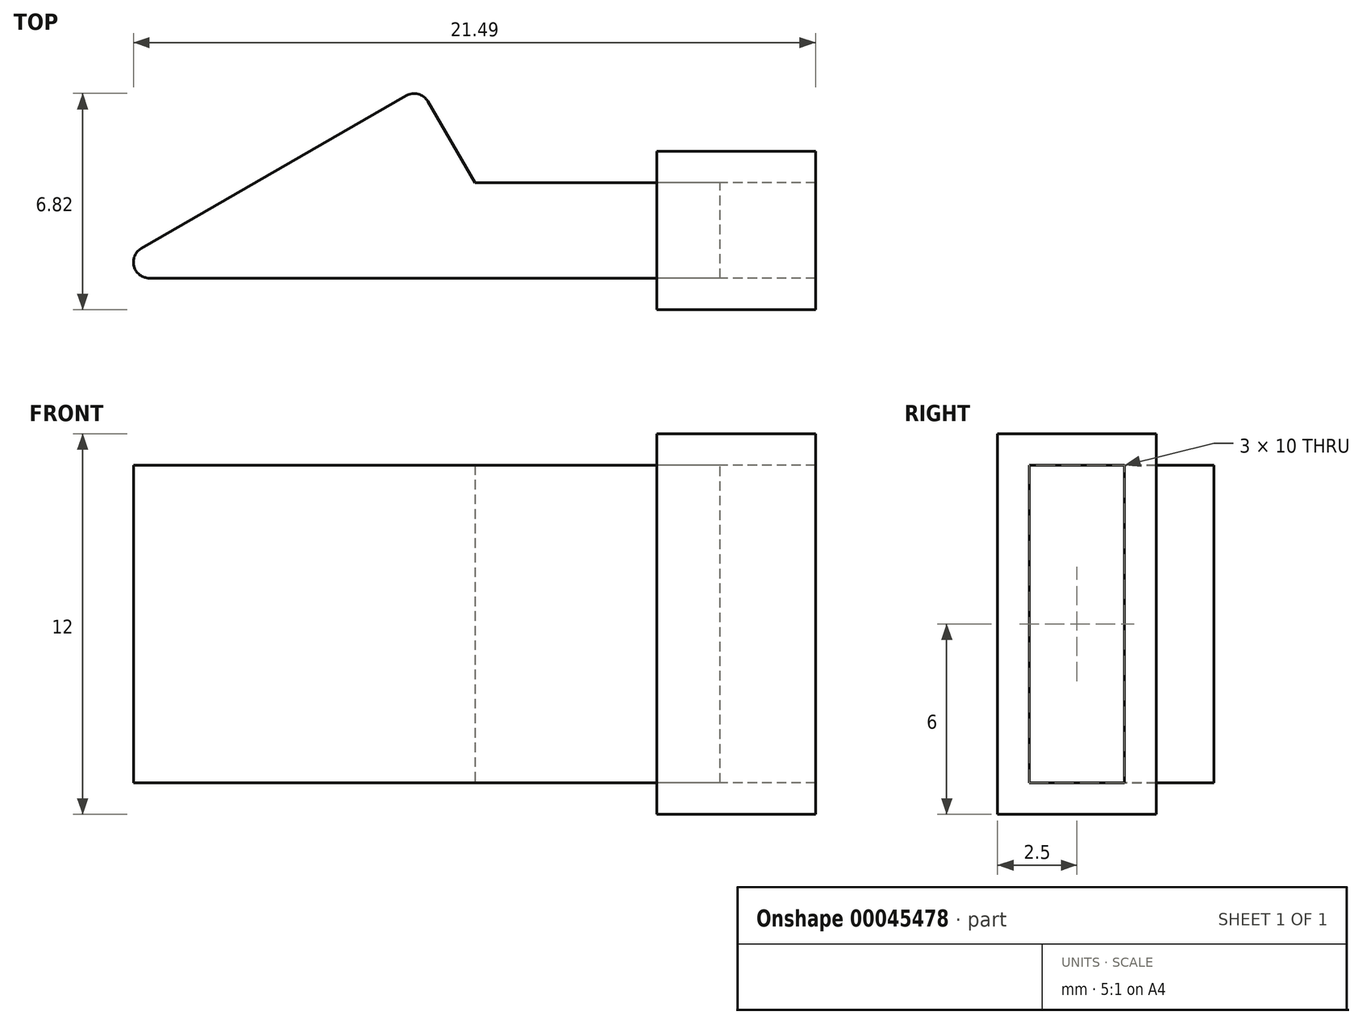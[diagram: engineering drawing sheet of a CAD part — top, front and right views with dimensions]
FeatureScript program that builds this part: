
annotation { "Feature Type Name" : "Feature", "Feature Type Description" : "" }
export const myFeature = defineFeature(function(context is Context, id is Id, definition is map)
    precondition{}
    {
        {
            var Q0;
            Q0=qCreatedBy(makeId("Top.planeOp"),FACE);
            var sketch = newSketch(context, id + "F0", { "sketchPlane" : qUnion([Q0])});
            skLineSegment(sketch, "E0", {"start": v(0, 0) * mm, "end": v(-13.86, 0) * mm});
            skLineSegment(sketch, "E1", {"start": v(-13.86, 0) * mm, "end": v(-3.46, 6) * mm});
            skLineSegment(sketch, "E2", {"start": v(-3.46, 6) * mm, "end": v(0, 0) * mm});
            skLineSegment(sketch, "E3", {"start": v(-3.46, 6) * mm, "end": v(-3.46, 0) * mm, "construction": true});
            skSolve(sketch);
        }
        {
            var Q0;
            Q0=qSketchRegion(id+"F0",true);
            extrude(context, id + "F1", {"entities" : qUnion([Q0]), "depth" : 10 * mm});
        }
        {
            var Q0;
            Q0=qCreatedBy(makeId("Right.planeOp"),FACE);
            cPlane(context, id + "F2", {"entities" : qUnion([Q0]), "cplaneType" : CPlaneType.OFFSET, "offset" : 3.46 * mm, "oppositeDirection" : true, "width" : 150 * mm, "height" : 150 * mm});
        }
        {
            var Q0;
            Q0=qCreatedBy(id+"F2.planeOp",FACE);
            var sketch = newSketch(context, id + "F3", { "sketchPlane" : qUnion([Q0])});
            skLineSegment(sketch, "E4.bottom", {"start": v(0, 0) * mm, "end": v(3, 0) * mm});
            skLineSegment(sketch, "E4.top", {"start": v(0, 10) * mm, "end": v(3, 10) * mm});
            skLineSegment(sketch, "E4.left", {"start": v(0, 0) * mm, "end": v(0, 10) * mm});
            skLineSegment(sketch, "E4.right", {"start": v(3, 0) * mm, "end": v(3, 10) * mm});
            skSolve(sketch);
        }
        {
            var Q0;
            Q0=qSketchRegion(id+"F3",true);
            extrude(context, id + "F4", {"entities" : qUnion([Q0]), "operationType" : NewBodyOperationType.ADD, "depth" : 9.46 * mm});
        }
        {
            var Q0;
            Q0=makeQuery(id+"F4.opExtrude","CAP_FACE",FACE,{"disambiguationData":[OSD([sQuery(id+"F3.wireOp",EDGE,"E4.bottom"),sQuery(id+"F3.wireOp",EDGE,"E4.top"),sQuery(id+"F3.wireOp",EDGE,"E4.left"),sQuery(id+"F3.wireOp",EDGE,"E4.right")])],"isStart":false});
            var sketch = newSketch(context, id + "F5", { "sketchPlane" : qUnion([Q0])});
            skLineSegment(sketch, "E5.bottom", {"start": v(0, 10) * mm, "end": v(3, 10) * mm});
            skLineSegment(sketch, "E5.top", {"start": v(0, 0) * mm, "end": v(3, 0) * mm});
            skLineSegment(sketch, "E5.left", {"start": v(0, 10) * mm, "end": v(0, 0) * mm});
            skLineSegment(sketch, "E5.right", {"start": v(3, 10) * mm, "end": v(3, 0) * mm});
            skLineSegment(sketch, "E6.bottom", {"start": v(-1, 11) * mm, "end": v(4, 11) * mm});
            skLineSegment(sketch, "E6.top", {"start": v(-1, -1) * mm, "end": v(4, -1) * mm});
            skLineSegment(sketch, "E6.left", {"start": v(-1, 11) * mm, "end": v(-1, -1) * mm});
            skLineSegment(sketch, "E6.right", {"start": v(4, 11) * mm, "end": v(4, -1) * mm});
            skSolve(sketch);
        }
        {
            var Q0;
            Q0=makeQuery(id+"F5.imprint","IMPRINT",FACE,{"disambiguationData":[TD([[makeQuery(id+"F5.imprint","IMPRINT",EDGE,{"derivedFrom":sQuery(id+"F5.wireOp",EDGE,"E5.bottom")}),1.0]])]});
            extrude(context, id + "F6", {"entities" : qUnion([Q0]), "depth" : 3 * mm, "hasSecondDirection" : true, "secondDirectionOppositeDirection" : true, "secondDirectionDepth" : 2 * mm});
        }
        {
            var Q0;
            Q0=makeQuery(id+"F1.opExtrude","SWEPT_EDGE",EDGE,{"disambiguationData":[OSD([sQuery(id+"F0.wireOp",EDGE,"E0"),sQuery(id+"F0.wireOp",EDGE,"E1")])]});
            var Q1;
            Q1=makeQuery(id+"F1.opExtrude","SWEPT_EDGE",EDGE,{"disambiguationData":[OSD([sQuery(id+"F0.wireOp",EDGE,"E1"),sQuery(id+"F0.wireOp",EDGE,"E2")])]});
            fillet(context, id + "F7", {"entities" : qUnion([Q0, Q1]), "radius" : .5 * mm, "tangentPropagation" : true, "allowEdgeOverflow" : false});
        }
    });
